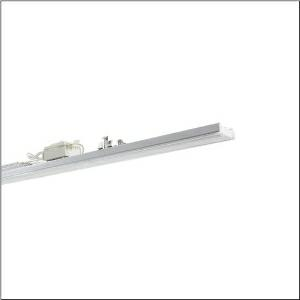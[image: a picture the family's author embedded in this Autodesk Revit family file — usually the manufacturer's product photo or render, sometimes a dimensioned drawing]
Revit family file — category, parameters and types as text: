
# Revit family: licross_11_recessed_mo_51tl1ede445g
name_source: partatom
category: Lighting Fixtures
units: mm (PartAtom-declared; Revit-internal decimal feet)

## family parameters
Cut with Voids When Loaded = No
Host = Face
Light Source = No
Part Type = Normal
Room Calculation Point = No
Round Connector Dimension = Use Diameter
Shared = No

## types (1)
- --- (1 x LED, 4950 lm, 29.6 W, 4000K)
    Apparent Load = 30 VA
    CIE Flux Codes = 85 95 99 100 100
    Color Rendering = 80
    Color Temperature = 4000K
    Default Elevation = 1800 mm
    Description = Licross 11 Recessed MO, luminaire insert, of sheet steel, coil coated, white, length: 750mm, width: 66mm, height: 67mm, LED rated luminous flux: 4.950lm, light colour: 840, SDCM (Standard Deviation of Colour Matching)MacAdam ≤ 2 SDCM (initial), control gear: DALI 2, with plug, 5-pole, with phase selection, mains connection: 220..240V, AC, 50/60Hz, rated input power: 30W, internal wiring halogen-free, primary light control with lens, of plastic, primary optical cover: cover, of PMMA, light emission: direct distribution, primary light characteristic: symmetric, protection rating (complete): IP40, insulation class (complete): insulation class I (protective earthing), certification: CE, ENEC, VDE, UKCA, protection symbol: D if used in an environment without relevant dust loads with corresponding accessories, impact resistance: IK06, permissible ambient temperature for indoor applications: -25..+35°C, corresponds to IFS (International Featured Standards) requirements for safety and quality in the food industry, reducing of maximum allowable ambient temperature of 5°C with ceiling mounting, LABS conformity tested according to VDMA 24364:2018-05, The light source and the operating device comply with the requirements of the Ecodesign Regulation (EU) 2019/2020 and are replaceable in accordance with this regulation, packaging unit: 1 piece
    Height = 58 mm
    Lamp = 1 x LED
    Lamp Light Flux = 4950 lm
    Lamp Power = 29.6 W
    Lamp count = 1
    Length = 750 mm
    Luminous efficacy = 167 lm/W
    Manufacturer = Siteco
    ModVariant = No
    Model = 51TL1EDE445G
    Mounting Place = Ceiling
    Mounting Type = Pendant
    Number of Poles = 1
    OnlyDefault = Yes
    Power Factor = 1
    Product Name = Licross 11 Recessed MO
    Product group = luminaire insert | ceiling pendant
    ProductGroupID = 901
    Protection Class = Protection class I
    Protection Degree = IP 40
    RLX_Detail_Level = 1
    RLX_Emergency_Light_Flux = 0 lm
    RLX_Emergency_Type = 0
    RLX_Emergency_Type_DB = No
    RlxData = <blob elided: 29529 chars, md5=2e320098>
    Socket = socket
    Standby Power = 0 W
    System Light Flux = 4950 lm
    System Power = 30 W
    Type Comments = factory setting: luminous flux: 100 % | dim-lin: 254 | 378 mA
    Type Image = l_1296930.jpg
    URL = http://relux.com
    VarID = @adj_099479
    Voltage = 0 V
    Weight = 0.00 kg
    Width = 66 mm

## geometry (parser evidence)
native form markers: Blend x4, Sweep x8
no freeform markers — native parametric forms only
